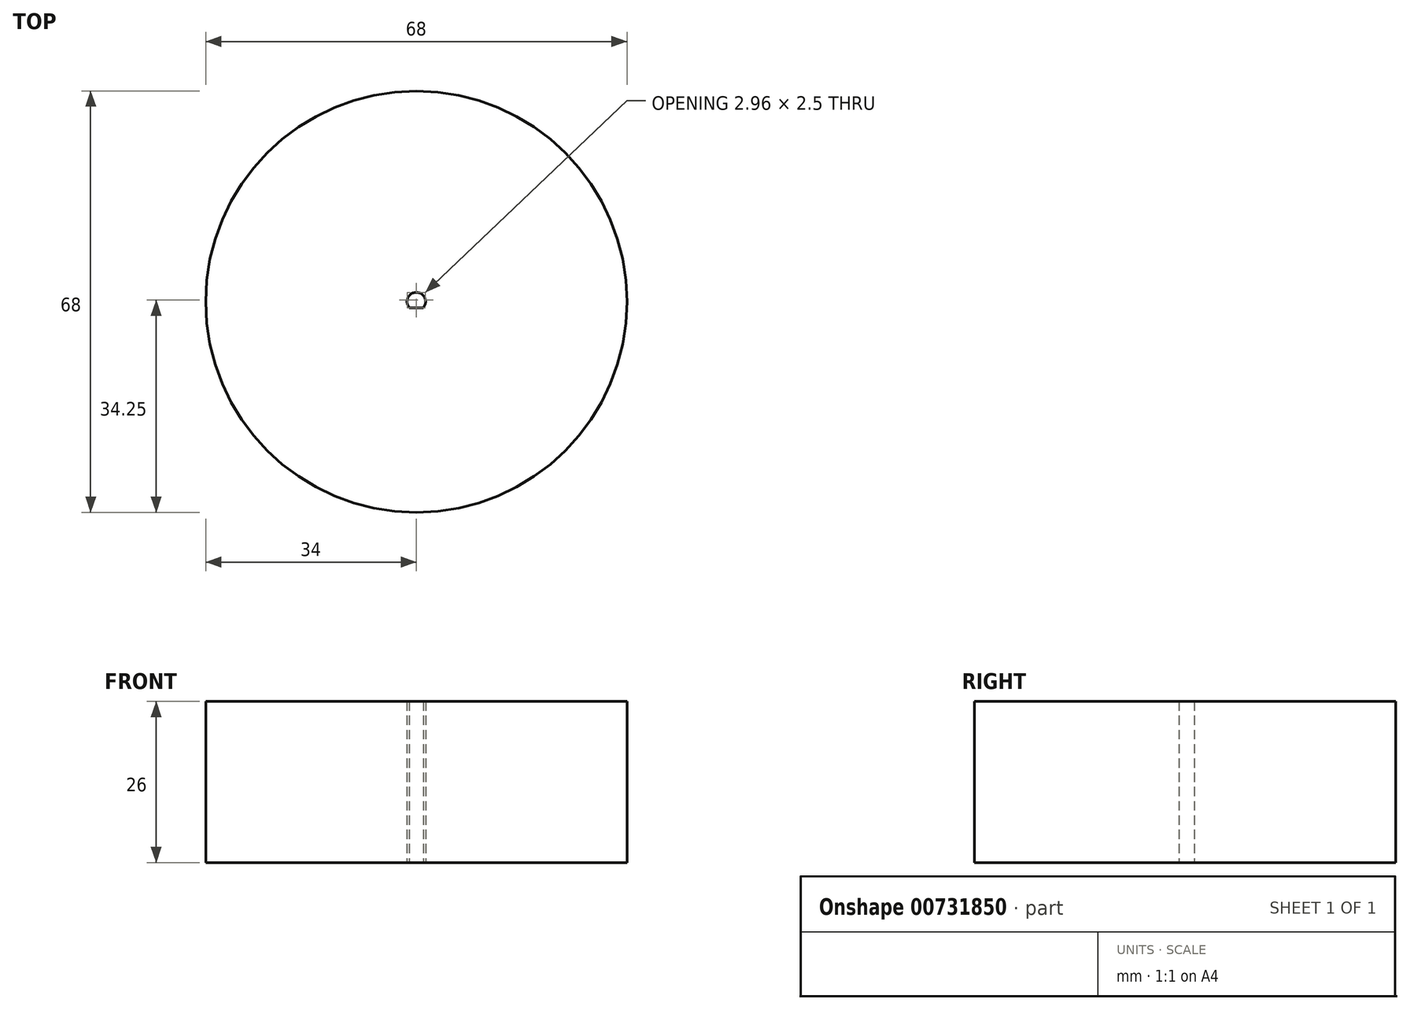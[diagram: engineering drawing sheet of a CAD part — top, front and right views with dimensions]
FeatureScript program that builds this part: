
annotation { "Feature Type Name" : "Feature", "Feature Type Description" : "" }
export const myFeature = defineFeature(function(context is Context, id is Id, definition is map)
    precondition{}
    {
        {
            var Q0;
            Q0=qCreatedBy(makeId("Top.planeOp"),FACE);
            var sketch = newSketch(context, id + "F0", { "sketchPlane" : qUnion([Q0])});
            skCircle(sketch, "E0", {"center": v(0, 0) * mm, "radius": 34 * mm});
            skSolve(sketch);
        }
        {
            var Q0;
            Q0=makeQuery(id+"F0.imprint","IMPRINT",FACE,{"disambiguationData":[TD([[makeQuery(id+"F0.imprint","IMPRINT",EDGE,{"derivedFrom":sQuery(id+"F0.wireOp",EDGE,"E0")}),1.0]])]});
            var sketch = newSketch(context, id + "F1", { "sketchPlane" : qUnion([Q0])});
            skArc(sketch, "E1", {"start": v(1.12, -1) * mm, "mid": v(0, 1.5) * mm, "end": v(-1.12, -1) * mm});
            skLineSegment(sketch, "E2", {"start": v(-1.12, -1) * mm, "end": v(1.12, -1) * mm});
            skPoint(sketch, "E3.orphan", {"position": v(0, 1.5) * mm});
            skPoint(sketch, "E4.end.orphan", {"position": v(0, -1) * mm});
            skSolve(sketch);
        }
        {
            var Q0;
            Q0=makeQuery(id+"F1.imprint","IMPRINT",FACE,{"disambiguationData":[TD([[makeQuery(id+"F1.imprint","IMPRINT",EDGE,{"derivedFrom":sQuery(id+"F1.wireOp",EDGE,"E1")}),-1.0]])]});
            extrude(context, id + "F2", {"entities" : qUnion([Q0]), "depth" : 26 * mm, "offsetDistance" : 25 * mm});
        }
    });
